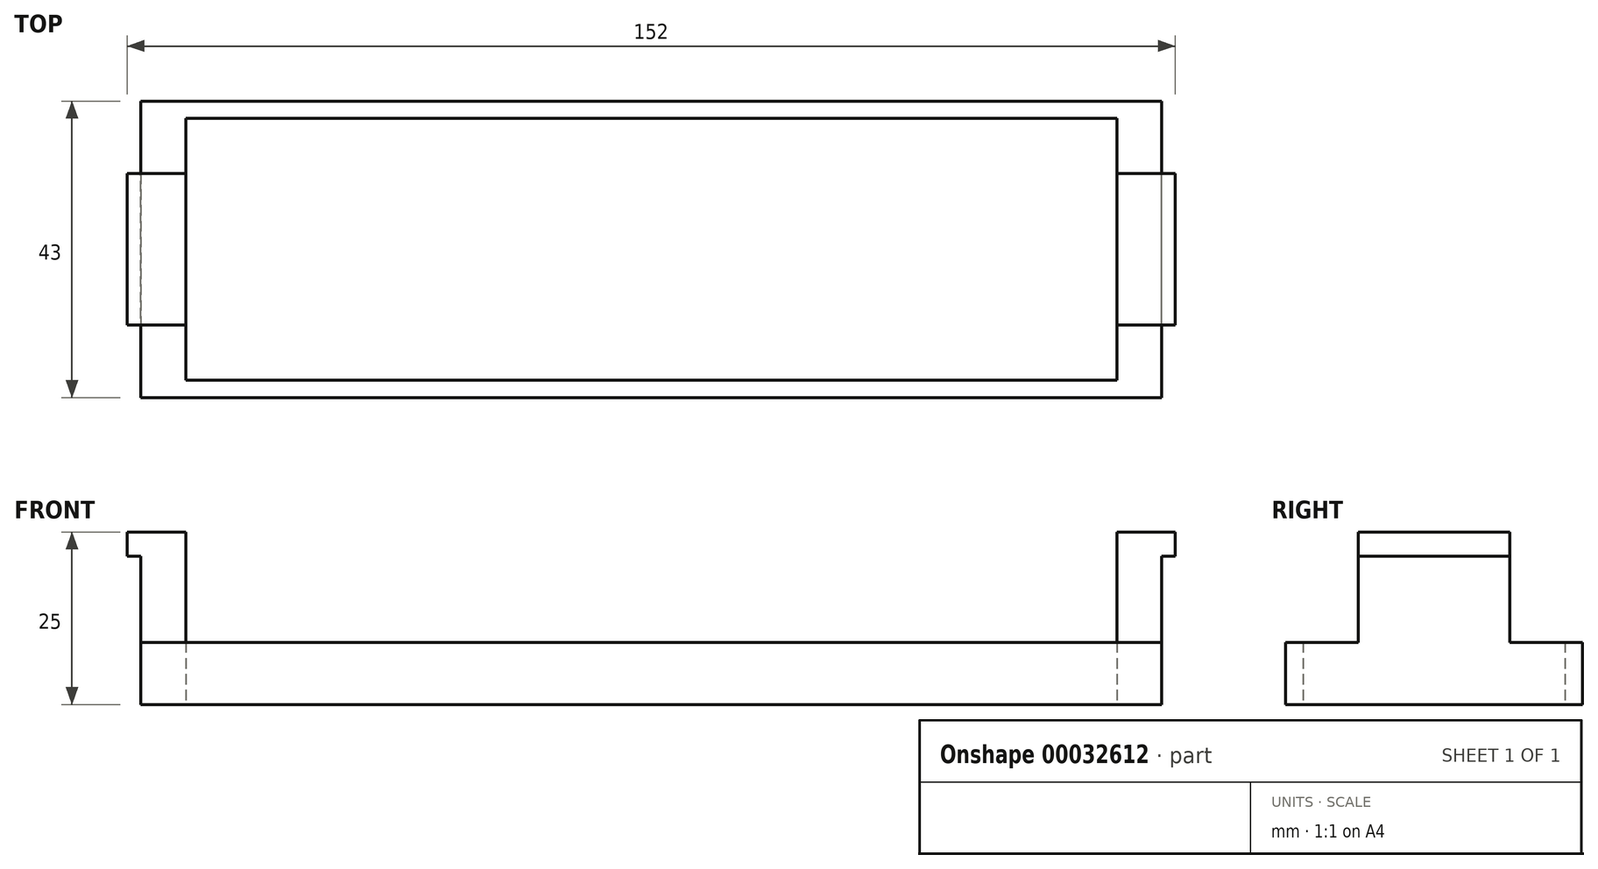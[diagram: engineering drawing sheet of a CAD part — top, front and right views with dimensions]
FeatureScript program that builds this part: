
annotation { "Feature Type Name" : "Feature", "Feature Type Description" : "" }
export const myFeature = defineFeature(function(context is Context, id is Id, definition is map)
    precondition{}
    {
        {
            var Q0;
            Q0=qCreatedBy(makeId("Top.planeOp"),FACE);
            var sketch = newSketch(context, id + "F0", { "sketchPlane" : qUnion([Q0])});
            skLineSegment(sketch, "E0.bottom", {"start": v(-74, -21.5) * mm, "end": v(74, -21.5) * mm});
            skLineSegment(sketch, "E0.top", {"start": v(-74, 21.5) * mm, "end": v(74, 21.5) * mm});
            skLineSegment(sketch, "E0.left", {"start": v(-74, -21.5) * mm, "end": v(-74, 21.5) * mm});
            skLineSegment(sketch, "E0.right", {"start": v(74, -21.5) * mm, "end": v(74, 21.5) * mm});
            skPoint(sketch, "E0.middle", {"position": v(0, 0) * mm});
            skLineSegment(sketch, "E1.bottom", {"start": v(-67.5, -19) * mm, "end": v(67.5, -19) * mm});
            skLineSegment(sketch, "E1.top", {"start": v(-67.5, 19) * mm, "end": v(67.5, 19) * mm});
            skLineSegment(sketch, "E1.left", {"start": v(-67.5, -19) * mm, "end": v(-67.5, 19) * mm});
            skLineSegment(sketch, "E1.right", {"start": v(67.5, -19) * mm, "end": v(67.5, 19) * mm});
            skSolve(sketch);
        }
        {
            var Q0;
            Q0=makeQuery(id+"F0.imprint","IMPRINT",FACE,{"disambiguationData":[TD([[makeQuery(id+"F0.imprint","IMPRINT",EDGE,{"derivedFrom":sQuery(id+"F0.wireOp",EDGE,"E0.bottom")}),1.0]])]});
            extrude(context, id + "F1", {"entities" : qUnion([Q0]), "depth" : 9 * mm});
        }
        {
            var Q0;
            Q0=makeQuery(id+"F1.opExtrude","CAP_FACE",FACE,{"disambiguationData":[OSD([sQuery(id+"F0.wireOp",EDGE,"E0.bottom"),sQuery(id+"F0.wireOp",EDGE,"E0.top"),sQuery(id+"F0.wireOp",EDGE,"E0.left"),sQuery(id+"F0.wireOp",EDGE,"E0.right")])],"isStart":false});
            var sketch = newSketch(context, id + "F2", { "sketchPlane" : qUnion([Q0])});
            skLineSegment(sketch, "E2.bottom", {"start": v(-67.5, -11) * mm, "end": v(-80.5, -11) * mm});
            skLineSegment(sketch, "E2.top", {"start": v(-67.5, 11) * mm, "end": v(-80.5, 11) * mm});
            skLineSegment(sketch, "E2.left", {"start": v(-67.5, -11) * mm, "end": v(-67.5, 11) * mm});
            skLineSegment(sketch, "E2.right", {"start": v(-80.5, -11) * mm, "end": v(-80.5, 11) * mm});
            skPoint(sketch, "E2.middle", {"position": v(-74, 0) * mm});
            skLineSegment(sketch, "E3.bottom", {"start": v(67.5, -11) * mm, "end": v(80.5, -11) * mm});
            skLineSegment(sketch, "E3.top", {"start": v(67.5, 11) * mm, "end": v(80.5, 11) * mm});
            skLineSegment(sketch, "E3.left", {"start": v(67.5, -11) * mm, "end": v(67.5, 11) * mm});
            skLineSegment(sketch, "E3.right", {"start": v(80.5, -11) * mm, "end": v(80.5, 11) * mm});
            skPoint(sketch, "E3.middle", {"position": v(74, 0) * mm});
            skLineSegment(sketch, "E4", {"start": v(-74, 11) * mm, "end": v(-74, -11) * mm});
            skLineSegment(sketch, "E5", {"start": v(74, 11) * mm, "end": v(74, -11) * mm});
            skSolve(sketch);
        }
        {
            var Q0;
            {var subQ0=sQuery(id+"F2.wireOp",EDGE,"E2.left");Q0=makeQuery(id+"F2.imprint","IMPRINT",FACE,{"disambiguationData":[TD([[makeQuery(id+"F2.imprint","IMPRINT",EDGE,{"derivedFrom":subQ0}),1.0]])]});}
            var Q1;
            {var subQ0=sQuery(id+"F2.wireOp",EDGE,"E3.left");Q1=makeQuery(id+"F2.imprint","IMPRINT",FACE,{"disambiguationData":[TD([[makeQuery(id+"F2.imprint","IMPRINT",EDGE,{"derivedFrom":subQ0}),-1.0]])]});}
            extrude(context, id + "F3", {"entities" : qUnion([Q0, Q1]), "operationType" : NewBodyOperationType.ADD, "depth" : 16 * mm});
        }
        {
            var Q0;
            Q0=makeQuery(id+"F3.boolean.opBoolean","MERGE",FACE,{"derivedFrom":[makeQuery(id+"F1.opExtrude","SWEPT_FACE",FACE,{"disambiguationData":[OSD([sQuery(id+"F0.wireOp",EDGE,"E0.left")])]}),makeQuery(id+"F3.opExtrude","SWEPT_FACE",FACE,{"disambiguationData":[OSD([sQuery(id+"F2.wireOp",EDGE,"E4")])]})]});
            var sketch = newSketch(context, id + "F4", { "sketchPlane" : qUnion([Q0])});
            skLineSegment(sketch, "E6.bottom", {"start": v(-11, 25) * mm, "end": v(11, 25) * mm});
            skLineSegment(sketch, "E6.top", {"start": v(-11, 21.5) * mm, "end": v(11, 21.5) * mm});
            skLineSegment(sketch, "E6.left", {"start": v(-11, 25) * mm, "end": v(-11, 21.5) * mm});
            skLineSegment(sketch, "E6.right", {"start": v(11, 25) * mm, "end": v(11, 21.5) * mm});
            skSolve(sketch);
        }
        {
            var Q0;
            Q0=makeQuery(id+"F4.imprint","IMPRINT",FACE,{"disambiguationData":[TD([[makeQuery(id+"F4.imprint","IMPRINT",EDGE,{"derivedFrom":sQuery(id+"F4.wireOp",EDGE,"E6.bottom")}),1.0]])]});
            extrude(context, id + "F5", {"entities" : qUnion([Q0]), "operationType" : NewBodyOperationType.ADD, "depth" : 2 * mm});
        }
        {
            var Q0;
            Q0=makeQuery(id+"F3.boolean.opBoolean","MERGE",FACE,{"derivedFrom":[makeQuery(id+"F1.opExtrude","SWEPT_FACE",FACE,{"disambiguationData":[OSD([sQuery(id+"F0.wireOp",EDGE,"E0.right")])]}),makeQuery(id+"F3.opExtrude","SWEPT_FACE",FACE,{"disambiguationData":[OSD([sQuery(id+"F2.wireOp",EDGE,"E5")])]})]});
            var sketch = newSketch(context, id + "F6", { "sketchPlane" : qUnion([Q0])});
            skLineSegment(sketch, "E7.bottom", {"start": v(-11, 25) * mm, "end": v(11, 25) * mm});
            skLineSegment(sketch, "E7.top", {"start": v(-11, 21.5) * mm, "end": v(11, 21.5) * mm});
            skLineSegment(sketch, "E7.left", {"start": v(-11, 25) * mm, "end": v(-11, 21.5) * mm});
            skLineSegment(sketch, "E7.right", {"start": v(11, 25) * mm, "end": v(11, 21.5) * mm});
            skSolve(sketch);
        }
        {
            var Q0;
            Q0=makeQuery(id+"F6.imprint","IMPRINT",FACE,{"disambiguationData":[TD([[makeQuery(id+"F6.imprint","IMPRINT",EDGE,{"derivedFrom":sQuery(id+"F6.wireOp",EDGE,"E7.bottom")}),-1.0]])]});
            extrude(context, id + "F7", {"entities" : qUnion([Q0]), "operationType" : NewBodyOperationType.ADD, "depth" : 2 * mm});
        }
        {
            var Q0;
            Q0=makeQuery(id+"F1.opExtrude","SWEPT_BODY",BODY,{"disambiguationData":[OSD([sQuery(id+"F0.wireOp",EDGE,"E0.bottom"),sQuery(id+"F0.wireOp",EDGE,"E0.top"),sQuery(id+"F0.wireOp",EDGE,"E0.left"),sQuery(id+"F0.wireOp",EDGE,"E0.right"),sQuery(id+"F0.wireOp",EDGE,"E1.bottom"),sQuery(id+"F0.wireOp",EDGE,"E1.top"),sQuery(id+"F0.wireOp",EDGE,"E1.left"),sQuery(id+"F0.wireOp",EDGE,"E1.right")])]});
            transform(context, id + "F8", {"entities" : qUnion([Q0]), "transformType" : TransformType.TRANSLATION_3D, "dx" : 0 * mm, "dy" : 0 * mm, "dz" : 0 * mm, "makeCopy" : true});
        }
        {
            var Q0;
            Q0=makeQuery(id+"F1.opExtrude","SWEPT_BODY",BODY,{"disambiguationData":[OSD([sQuery(id+"F0.wireOp",EDGE,"E0.bottom"),sQuery(id+"F0.wireOp",EDGE,"E0.top"),sQuery(id+"F0.wireOp",EDGE,"E0.left"),sQuery(id+"F0.wireOp",EDGE,"E0.right"),sQuery(id+"F0.wireOp",EDGE,"E1.bottom"),sQuery(id+"F0.wireOp",EDGE,"E1.top"),sQuery(id+"F0.wireOp",EDGE,"E1.left"),sQuery(id+"F0.wireOp",EDGE,"E1.right")])]});
            deleteBodies(context, id + "F9", {"entities" : qUnion([Q0])});
        }
    });
